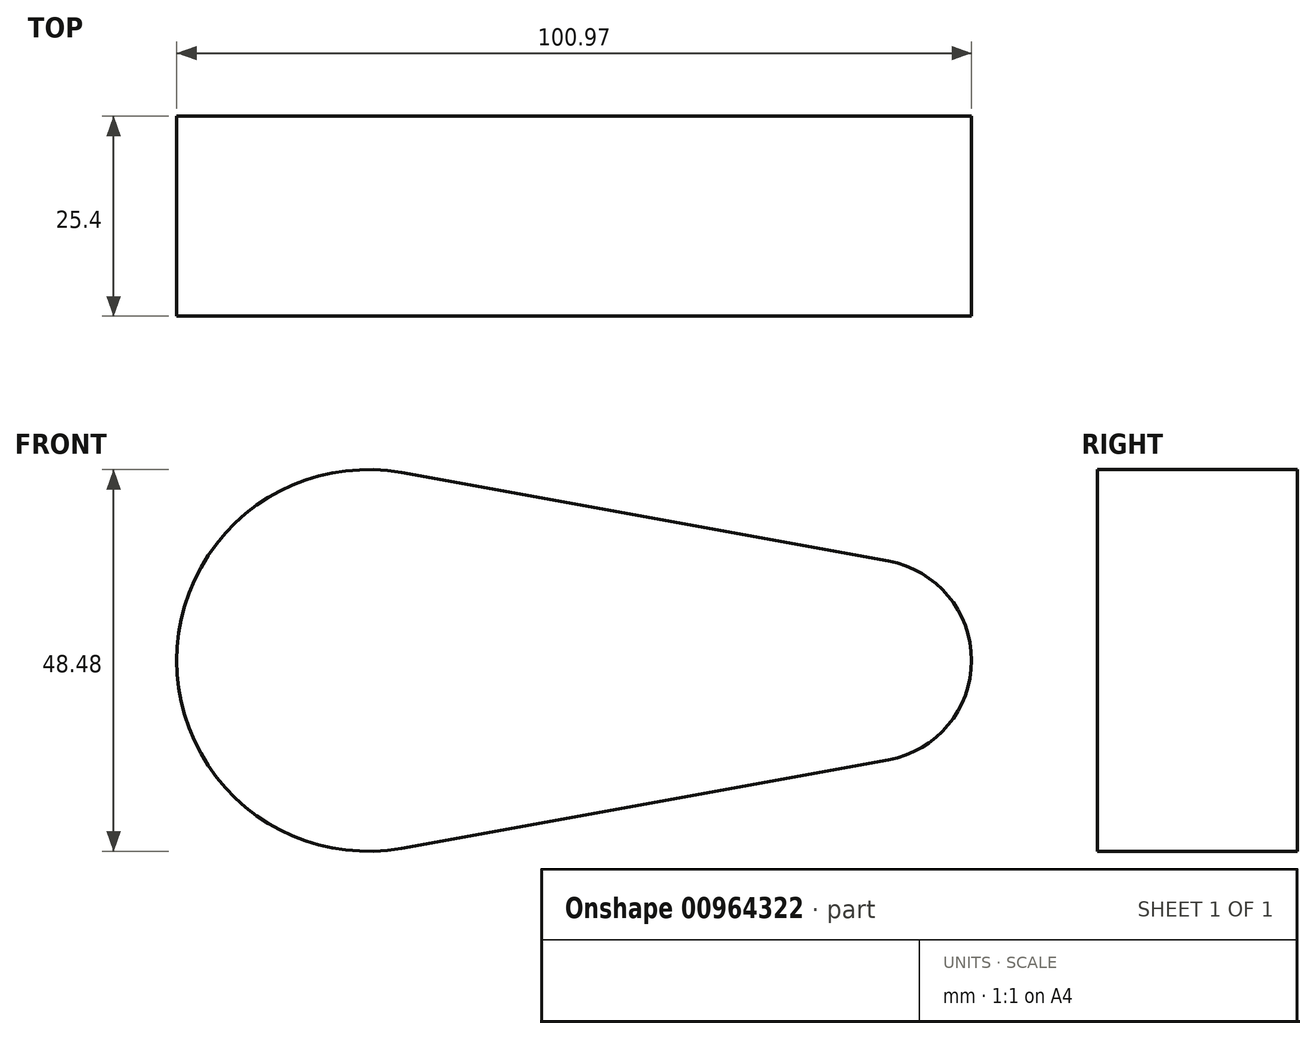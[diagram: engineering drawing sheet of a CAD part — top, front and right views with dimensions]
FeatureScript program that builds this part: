
annotation { "Feature Type Name" : "Feature", "Feature Type Description" : "" }
export const myFeature = defineFeature(function(context is Context, id is Id, definition is map)
    precondition{}
    {
        {
            var Q0;
            Q0=qCreatedBy(makeId("Front.planeOp"),FACE);
            var sketch = newSketch(context, id + "F0", { "sketchPlane" : qUnion([Q0])});
            skCircle(sketch, "E0", {"center": v(0, 0) * mm, "radius": 24.24 * mm});
            skCircle(sketch, "E1", {"center": v(63.9, 0) * mm, "radius": 12.82 * mm});
            skLineSegment(sketch, "E2", {"start": v(4.33, 23.85) * mm, "end": v(66.2, 12.62) * mm});
            skLineSegment(sketch, "E3", {"start": v(4.33, -23.85) * mm, "end": v(66.2, -12.62) * mm});
            skSolve(sketch);
        }
        {
            var Q0;
            Q0 = qSketchRegion(id + "F0", true);
            extrude(context, id + "F1", {"entities" : qUnion([Q0]), "depth" : 25.4 * mm, "offsetDistance" : 25.4 * mm});
        }
    });
